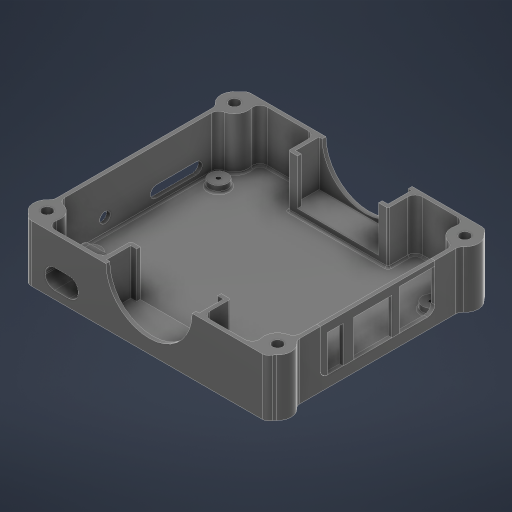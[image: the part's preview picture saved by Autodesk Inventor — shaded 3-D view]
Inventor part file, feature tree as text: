
AUTODESK INVENTOR PART (.ipt)
format: ipt  version: 2023 (Build 270158000, 158)  size: 890,368 bytes
history: native  units: in
note: dims shown in document units (in); Inventor stores cm internally (conversion verified against a paired STEP export)
features: sketch x21, extrude x19, reference x14, projected_geometry x11, other x5, plane x3, fillet x3, hole x2
ambient origin geometry x8: Origin, YZ Plane, XZ Plane, XY Plane, X Axis, Y Axis, Z Axis, Center Point
bodies: Solid1 (feature_tree), Solid2 (feature_tree), Solid3 (feature_tree), Solid4 (feature_tree)
feature tree (78):
  plane  "Work Plane1"
  extrude  "Extrusion1"  Depth=0.04in
  extrude  "Extrusion2"  Depth=0.5512in
  extrude  "Extrusion3"  Depth=0.065in
  extrude  "Extrusion4"  TaperAngle=0.0deg  [1 undecoded]
  extrude  "Extrusion5"  Depth=0.7874in TaperAngle=0.0deg
  extrude  "Extrusion6"  Depth=0.0787in TaperAngle=0.0deg
  sketch  "Sketch7"  dims[d16=0.1in d17=0.1181in d18=0.0in]
  plane  "Work Plane2"
  extrude  "Extrusion7"  Depth=0.1181in TaperAngle=0.0deg
  extrude  "Extrusion8"  Depth=0.1181in TaperAngle=0.0deg
  extrude  "Extrusion9"  Depth=0.1181in TaperAngle=0.0deg
  sketch  "Sketch10"  dims[d28=1.7853in d29=0.05in]
  plane  "Work Plane3"
  extrude  "Extrusion10"  Depth=0.05in
  extrude  "Extrusion11"  Depth=0.05in
  extrude  "Extrusion12"  Depth=1.7323in
  hole  "Hole1"  [1 undecoded]
  extrude  "Extrusion13"  Depth=0.1in
  fillet  "Fillet1"  Radius=0.1in
  extrude  "Extrusion14"  Depth=0.063in
  fillet  "Fillet2"  Radius=0.063in
  hole  "Hole2"  [1 undecoded]
  fillet  "Fillet3"  Radius=1.0in
  extrude  "Extrusion15"  Depth=1.7323in
  extrude  "Extrusion16"  Depth=1.0in TaperAngle=0.0deg
  extrude  "Extrusion17"  Depth=0.1in
  extrude  "Extrusion18"  Depth=0.063in
  extrude  "Extrusion19"  Depth=0.0079in
  sketch  "Sketch1"  dims[d0=0.04in d1=0.04in]
  reference  "Reference1"
  reference  "Reference2"
  sketch  "Sketch2"  dims[d2=0.5512in d3=0.5512in]
  projected_geometry  "Projected Loop1"
  sketch  "Sketch3"  dims[d5=0.065in d6=0.065in]
  sketch  "Sketch4"  dims[d7=0.065in d8=0.0in]
  reference  "Reference3"
  reference  "Reference4"
  reference  "Reference5"
  reference  "Reference6"
  sketch  "Sketch5"  dims[d9=0.065in d10=0.7874in d11=0.0in]
  reference  "Reference7"
  reference  "Reference8"
  reference  "Reference9"
  sketch  "Sketch6"  dims[d12=0.1969in d13=0.0in d14=0.0787in d15=0.0in]
  reference  "Reference10"
  reference  "Reference11"
  sketch  "Sketch8"  dims[d19=0.6378in d22=0.1181in d23=0.0in]
  projected_geometry  "Projected Loop2"
  sketch  "Sketch9"  dims[d24=0.05in d25=0.1181in d26=0.0in]
  sketch  "Sketch11"  dims[d30=0.15in d31=0.05in]
  sketch  "Sketch12"  dims[d32=1.7323in d33=0.8661in]
  sketch  "Sketch13"  dims[d34=0.4843in d35=1.0in d36=0.0in]
  sketch  "Sketch14"  dims[d45=1.0in d46=0.0in d47=0.1in d48=0.1in]
  projected_geometry  "Projected Loop3"
  projected_geometry  "Projected Loop4"
  sketch  "Sketch15"  dims[d49=0.063in d50=0.063in d51=0.063in]
  sketch  "Sketch17"  dims[d52=0.063in d53=1.4961in d54=1.0in d55=0.0in]
  sketch  "Sketch18"  dims[d56=0.4724in d57=1.7323in]
  projected_geometry  "Projected Loop5"
  sketch  "Sketch19"  dims[d58=0.8661in d59=1.0in d60=0.0in]
  projected_geometry  "Projected Loop6"
  sketch  "Sketch20"  dims[d62=0.063in d63=0.1in]
  projected_geometry  "Projected Loop7"
  projected_geometry  "Projected Loop8"
  projected_geometry  "Projected Loop9"
  projected_geometry  "Projected Loop10"
  sketch  "Sketch21"  dims[d64=0.063in d65=0.063in]
  projected_geometry  "Projected Loop11"
  sketch  "Sketch22"  dims[d66=0.063in d67=0.1in d68=1.0in d69=0.0in d70=1.4961in d71=1.0in d72=0.0in d73=0.0793in d74=0.197in d75=0.173in d76=0.079in d77=0.5635in d78=1.0in d79=0.8108in d80=0.0394in d81=0.625in d82=0.0in d83=0.125in d84=3.25in d85=4.0in d86=0.4724in d87=0.1969in d88=0.0in d89=0.125in d90=0.177in d91=0.75in d92=0.313in d93=0.75in d94=0.5635in d95=1.0in d96=0.8108in d97=0.0312in d98=0.0079in d99=0.0in d100=0.0079in d101=0.0in d102=0.0079in d103=0.0in d104=0.0079in d105=0.0in d106=0.1875in d107=1.0in d108=0.0in]
  reference  "Reference12"
  reference  "Reference13"
  reference  "Reference14"
  other  "OrangePICover.iam"
  other  "OPi5_pcb_asm-0809:1"
  other  "orangepicover-002:1"
  other  "OPi5_pcb_asm-0809:2"
  other  "Assembly10"
note: 3 required parameter values undecoded (feature->parameter linkage not recoverable at this tier; creation-order binding heuristic only, values carry confidence <= 0.55)
